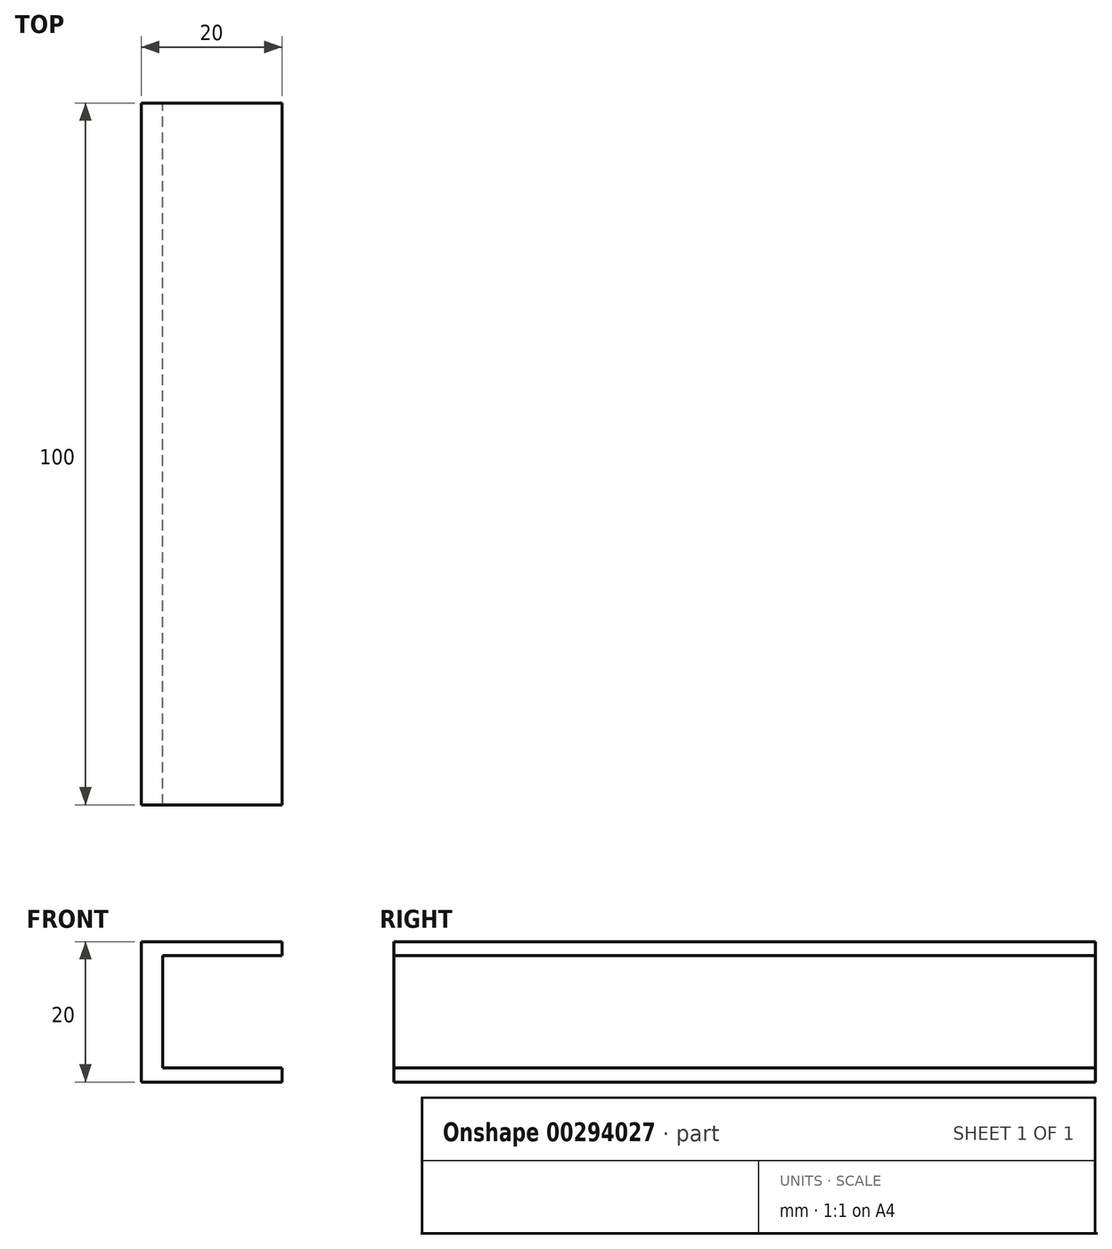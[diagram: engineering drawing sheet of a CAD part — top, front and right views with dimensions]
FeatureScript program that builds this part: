
annotation { "Feature Type Name" : "Feature", "Feature Type Description" : "" }
export const myFeature = defineFeature(function(context is Context, id is Id, definition is map)
    precondition{}
    {
        {
            var Q0;
            Q0=qCreatedBy(makeId("Front.planeOp"),FACE);
            var sketch = newSketch(context, id + "F0", { "sketchPlane" : qUnion([Q0])});
            skLineSegment(sketch, "E0.bottom", {"start": v(10, 10) * mm, "end": v(-10, 10) * mm});
            skLineSegment(sketch, "E0.top", {"start": v(10, -10) * mm, "end": v(-10, -10) * mm});
            skLineSegment(sketch, "E0.left", {"start": v(10, 10) * mm, "end": v(10, 8) * mm});
            skLineSegment(sketch, "E0.right", {"start": v(-10, 10) * mm, "end": v(-10, -10) * mm});
            skPoint(sketch, "E0.middle", {"position": v(0, 0) * mm});
            skLineSegment(sketch, "E1", {"start": v(10, 8) * mm, "end": v(-7, 8) * mm});
            skLineSegment(sketch, "E2", {"start": v(-7, 8) * mm, "end": v(-7, -8) * mm});
            skLineSegment(sketch, "E3", {"start": v(-7, -8) * mm, "end": v(10, -8) * mm});
            skLineSegment(sketch, "E4.trimOffspring", {"start": v(10, -8) * mm, "end": v(10, -10) * mm});
            skSolve(sketch);
        }
        {
            var Q0;
            Q0 = qSketchRegion(id + "F0", true);
            extrude(context, id + "F1", {"entities" : qUnion([Q0]), "depth" : 100 * mm});
        }
    });
